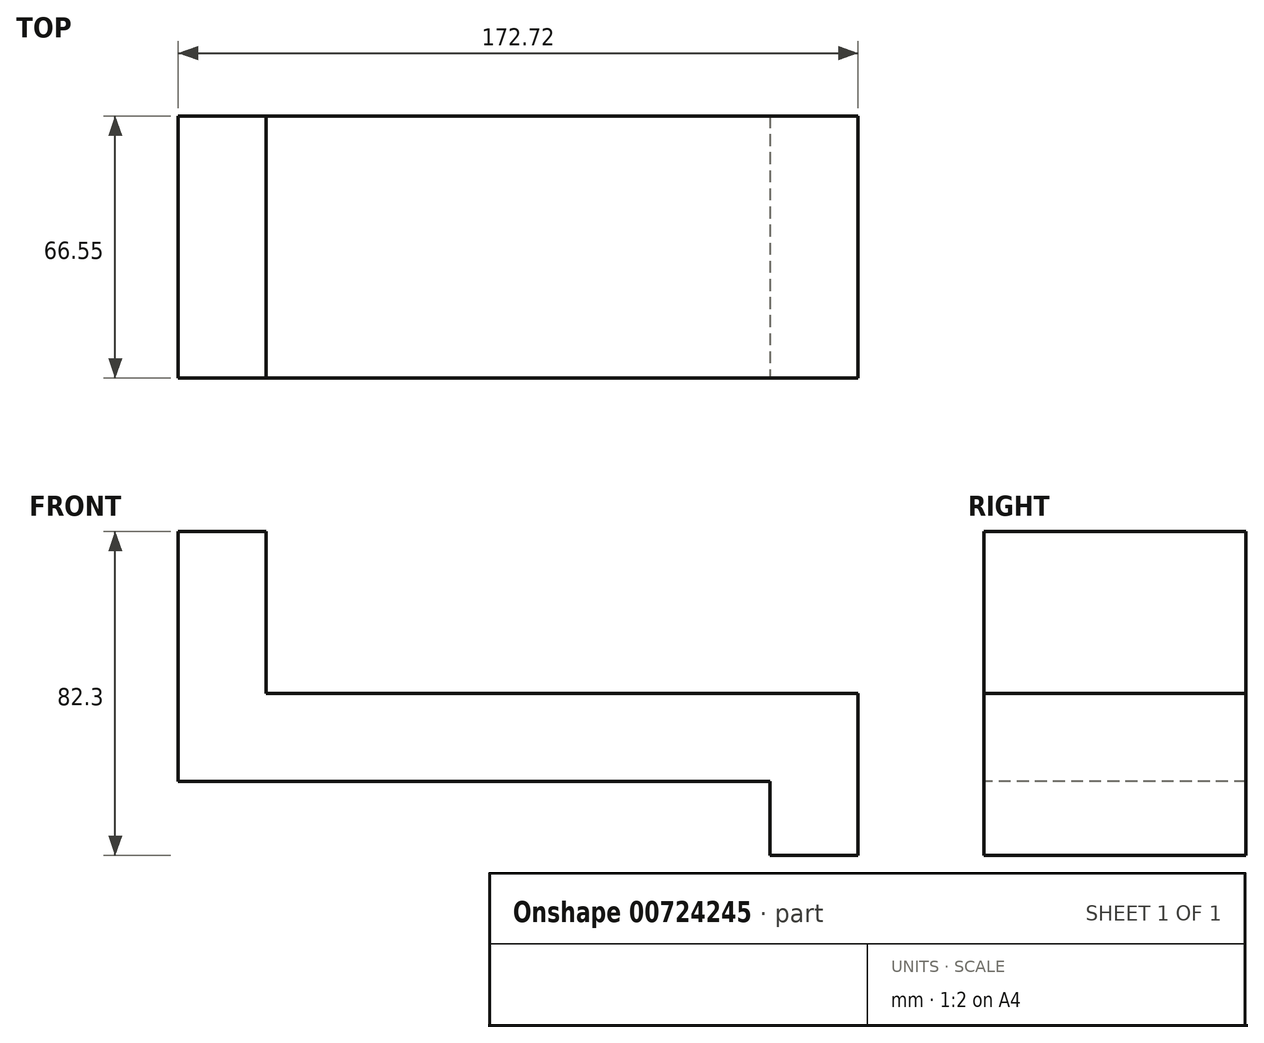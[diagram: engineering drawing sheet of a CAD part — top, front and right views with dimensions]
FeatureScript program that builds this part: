
annotation { "Feature Type Name" : "Feature", "Feature Type Description" : "" }
export const myFeature = defineFeature(function(context is Context, id is Id, definition is map)
    precondition{}
    {
        {
            var Q0;
            Q0=qCreatedBy(makeId("Front.planeOp"),FACE);
            var sketch = newSketch(context, id + "F0", { "sketchPlane" : qUnion([Q0])});
            skLineSegment(sketch, "E0", {"start": v(-77.94, 71.48) * mm, "end": v(-77.94, 7.98) * mm});
            skLineSegment(sketch, "E1", {"start": v(-77.94, 7.98) * mm, "end": v(72.43, 7.98) * mm});
            skLineSegment(sketch, "E2", {"start": v(72.43, 7.98) * mm, "end": v(72.43, -10.82) * mm});
            skLineSegment(sketch, "E3", {"start": v(-77.94, 71.48) * mm, "end": v(-55.59, 71.48) * mm});
            skLineSegment(sketch, "E4", {"start": v(-55.59, 71.48) * mm, "end": v(-55.59, 30.33) * mm});
            skLineSegment(sketch, "E5", {"start": v(94.78, 30.33) * mm, "end": v(-55.59, 30.33) * mm});
            skLineSegment(sketch, "E6", {"start": v(94.78, 30.33) * mm, "end": v(94.78, -10.82) * mm});
            skLineSegment(sketch, "E7", {"start": v(72.43, -10.82) * mm, "end": v(94.78, -10.82) * mm});
            skSolve(sketch);
        }
        {
            var Q0;
            Q0 = qSketchRegion(id + "F0", true);
            extrude(context, id + "F1", {"entities" : qUnion([Q0]), "oppositeDirection" : true, "depth" : 66.55 * mm, "offsetDistance" : 25.4 * mm});
        }
    });
